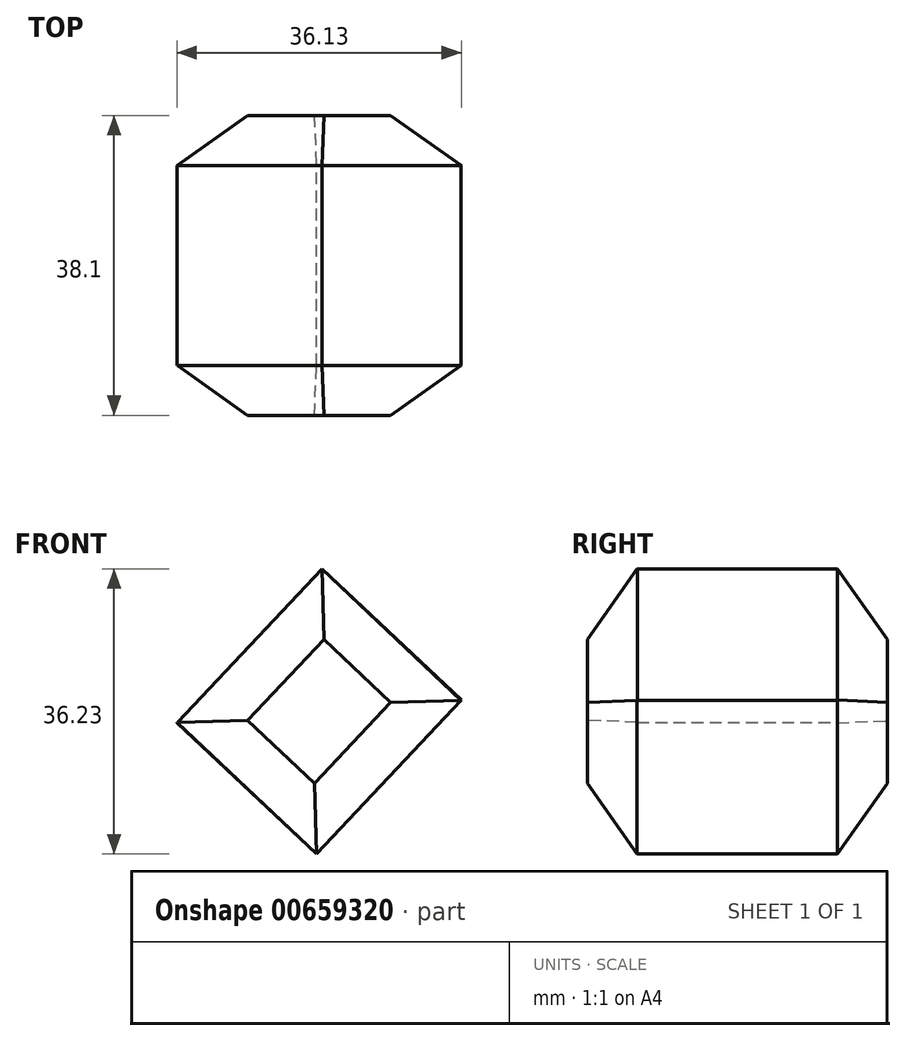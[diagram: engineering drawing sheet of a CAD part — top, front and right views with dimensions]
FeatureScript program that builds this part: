
annotation { "Feature Type Name" : "Feature", "Feature Type Description" : "" }
export const myFeature = defineFeature(function(context is Context, id is Id, definition is map)
    precondition{}
    {
        {
            var Q0;
            Q0=qCreatedBy(makeId("Front.planeOp"),FACE);
            var sketch = newSketch(context, id + "F0", { "sketchPlane" : qUnion([Q0])});
            skCircle(sketch, "E0", {"center": v(-16.93, -16.93) * mm, "radius": 23.2 * mm});
            skSolve(sketch);
        }
        {
            var Q0;
            Q0=makeQuery(id+"F0.imprint","IMPRINT",FACE,{"disambiguationData":[TD([[makeQuery(id+"F0.imprint","IMPRINT",EDGE,{"derivedFrom":sQuery(id+"F0.wireOp",EDGE,"E0")}),1.0]])]});
            extrude(context, id + "F1", {"entities" : qUnion([Q0]), "depth" : 12.7 * mm, "offsetDistance" : 25.4 * mm});
        }
        {
            var Q0;
            Q0=makeQuery(id+"F1.opExtrude","CAP_FACE",FACE,{"disambiguationData":[OSD([sQuery(id+"F0.wireOp",EDGE,"E0")])],"isStart":true});
            var sketch = newSketch(context, id + "F2", { "sketchPlane" : qUnion([Q0])});
            skSolve(sketch);
        }
        {
            var Q0;
            Q0=qSketchRegion(id+"F2",true);
            var Q1;
            Q1=makeQuery(id+"F2.imprint","IMPRINT",FACE,{"disambiguationData":[TD([[makeQuery(id+"F2.imprint","IMPRINT",EDGE,{"derivedFrom":makeQuery(id+"F1.opExtrude","CAP_EDGE",EDGE,{"disambiguationData":[OSD([sQuery(id+"F0.wireOp",EDGE,"E0")])],"isStart":true})}),-1.0]])]});
            extrude(context, id + "F3", {"entities" : qUnion([Q0, Q1]), "operationType" : NewBodyOperationType.ADD, "depth" : 12.7 * mm, "offsetDistance" : 25.4 * mm});
        }
        {
            var Q0;
            Q0=makeQuery(id+"F3.opExtrude","CAP_FACE",FACE,{"disambiguationData":[OSD([sQuery(id+"F0.wireOp",EDGE,"E0")])],"isStart":false});
            var sketch = newSketch(context, id + "F4", { "sketchPlane" : qUnion([Q0])});
            skLineSegment(sketch, "E1", {"start": v(16.57, 1.2) * mm, "end": v(34.99, -18.36) * mm});
            skLineSegment(sketch, "E2", {"start": v(34.99, -18.36) * mm, "end": v(17.28, -35.04) * mm});
            skLineSegment(sketch, "E3", {"start": v(17.28, -35.04) * mm, "end": v(-1.14, -15.49) * mm});
            skLineSegment(sketch, "E4", {"start": v(-1.14, -15.49) * mm, "end": v(16.57, 1.2) * mm});
            skSolve(sketch);
        }
        {
            var Q0;
            Q0=makeQuery(id+"F1.opExtrude","CAP_FACE",FACE,{"disambiguationData":[OSD([sQuery(id+"F0.wireOp",EDGE,"E0")])],"isStart":false});
            var sketch = newSketch(context, id + "F5", { "sketchPlane" : qUnion([Q0])});
            skLineSegment(sketch, "E5", {"start": v(-16.59, 1.2) * mm, "end": v(1.14, -15.54) * mm});
            skLineSegment(sketch, "E6", {"start": v(1.14, -15.54) * mm, "end": v(-17.26, -35.04) * mm});
            skLineSegment(sketch, "E7", {"start": v(-17.26, -35.04) * mm, "end": v(-35, -18.3) * mm});
            skLineSegment(sketch, "E8", {"start": v(-35, -18.3) * mm, "end": v(-16.59, 1.2) * mm});
            skSolve(sketch);
        }
        {
            var Q0;
            Q0=makeQuery(id+"F4.imprint","IMPRINT",FACE,{"disambiguationData":[TD([[makeQuery(id+"F4.imprint","IMPRINT",EDGE,{"derivedFrom":sQuery(id+"F4.wireOp",EDGE,"E1")}),-1.0]])]});
            extrude(context, id + "F6", {"entities" : qUnion([Q0]), "operationType" : NewBodyOperationType.ADD, "depth" : 6.35 * mm, "offsetDistance" : 25.4 * mm});
        }
        {
            var Q0;
            Q0=makeQuery(id+"F5.imprint","IMPRINT",FACE,{"disambiguationData":[TD([[makeQuery(id+"F5.imprint","IMPRINT",EDGE,{"derivedFrom":sQuery(id+"F5.wireOp",EDGE,"E5")}),-1.0]])]});
            extrude(context, id + "F7", {"entities" : qUnion([Q0]), "operationType" : NewBodyOperationType.ADD, "depth" : 6.35 * mm, "offsetDistance" : 25.4 * mm});
        }
        {
            var Q0;
            Q0=makeQuery(id+"F6.opExtrude","CAP_FACE",FACE,{"disambiguationData":[OSD([sQuery(id+"F4.wireOp",EDGE,"E1"),sQuery(id+"F4.wireOp",EDGE,"E2"),sQuery(id+"F4.wireOp",EDGE,"E3"),sQuery(id+"F4.wireOp",EDGE,"E4")])],"isStart":false});
            chamfer(context, id + "F8", {"entities" : qUnion([Q0]), "width" : 6.35 * mm, "tangentPropagation" : true});
        }
        {
            var Q0;
            Q0=makeQuery(id+"F7.opExtrude","CAP_FACE",FACE,{"disambiguationData":[OSD([sQuery(id+"F5.wireOp",EDGE,"E5"),sQuery(id+"F5.wireOp",EDGE,"E6"),sQuery(id+"F5.wireOp",EDGE,"E7"),sQuery(id+"F5.wireOp",EDGE,"E8")])],"isStart":false});
            chamfer(context, id + "F9", {"entities" : qUnion([Q0]), "width" : 6.35 * mm, "tangentPropagation" : true});
        }
        {
            var Q0;
            {var subQ0=sQuery(id+"F0.wireOp",EDGE,"E0");var subQ1=makeQuery(id+"F1.opExtrude","CAP_FACE",FACE,{"disambiguationData":[OSD([subQ0])],"isStart":false});Q0=makeQuery(id+"F7.boolean.opBoolean","SPLIT",FACE,{"disambiguationData":[TD([subQ1,makeQuery(id+"FOe0SaatVae6QVj_1.opFillet","BLEND_FACE",FACE,{"disambiguationData":[OSD([subQ0]),TDD([makeQuery(id+"F1.opExtrude","CAP_EDGE",EDGE,{"disambiguationData":[OSD([subQ0])],"isStart":false})])]}),makeQuery(id+"F7.opExtrude","SWEPT_FACE",FACE,{"disambiguationData":[OSD([sQuery(id+"F5.wireOp",EDGE,"E5")])]}),makeQuery(id+"F7.opExtrude","SWEPT_FACE",FACE,{"disambiguationData":[OSD([sQuery(id+"F5.wireOp",EDGE,"E6")])]}),makeQuery(id+"F7.opExtrude","SWEPT_FACE",FACE,{"disambiguationData":[OSD([sQuery(id+"F5.wireOp",EDGE,"E8")])]})])],"derivedFrom":subQ1});}
            var Q1;
            {var subQ0=sQuery(id+"F0.wireOp",EDGE,"E0");var subQ1=makeQuery(id+"F1.opExtrude","CAP_FACE",FACE,{"disambiguationData":[OSD([subQ0])],"isStart":false});Q1=makeQuery(id+"F7.boolean.opBoolean","SPLIT",FACE,{"disambiguationData":[TD([subQ1,makeQuery(id+"FOe0SaatVae6QVj_1.opFillet","BLEND_FACE",FACE,{"disambiguationData":[OSD([subQ0]),TDD([makeQuery(id+"F1.opExtrude","CAP_EDGE",EDGE,{"disambiguationData":[OSD([subQ0])],"isStart":false})])]}),makeQuery(id+"F7.opExtrude","SWEPT_FACE",FACE,{"disambiguationData":[OSD([sQuery(id+"F5.wireOp",EDGE,"E5")])]}),makeQuery(id+"F7.opExtrude","SWEPT_FACE",FACE,{"disambiguationData":[OSD([sQuery(id+"F5.wireOp",EDGE,"E7")])]}),makeQuery(id+"F7.opExtrude","SWEPT_FACE",FACE,{"disambiguationData":[OSD([sQuery(id+"F5.wireOp",EDGE,"E8")])]})])],"derivedFrom":subQ1});}
            var Q2;
            {var subQ0=sQuery(id+"F0.wireOp",EDGE,"E0");var subQ1=makeQuery(id+"F1.opExtrude","CAP_FACE",FACE,{"disambiguationData":[OSD([subQ0])],"isStart":false});Q2=makeQuery(id+"F7.boolean.opBoolean","SPLIT",FACE,{"disambiguationData":[TD([subQ1,makeQuery(id+"FOe0SaatVae6QVj_1.opFillet","BLEND_FACE",FACE,{"disambiguationData":[OSD([subQ0]),TDD([makeQuery(id+"F1.opExtrude","CAP_EDGE",EDGE,{"disambiguationData":[OSD([subQ0])],"isStart":false})])]}),makeQuery(id+"F7.opExtrude","SWEPT_FACE",FACE,{"disambiguationData":[OSD([sQuery(id+"F5.wireOp",EDGE,"E6")])]}),makeQuery(id+"F7.opExtrude","SWEPT_FACE",FACE,{"disambiguationData":[OSD([sQuery(id+"F5.wireOp",EDGE,"E7")])]}),makeQuery(id+"F7.opExtrude","SWEPT_FACE",FACE,{"disambiguationData":[OSD([sQuery(id+"F5.wireOp",EDGE,"E8")])]})])],"derivedFrom":subQ1});}
            var Q3;
            {var subQ0=sQuery(id+"F0.wireOp",EDGE,"E0");var subQ1=makeQuery(id+"F1.opExtrude","CAP_FACE",FACE,{"disambiguationData":[OSD([subQ0])],"isStart":false});Q3=makeQuery(id+"F7.boolean.opBoolean","SPLIT",FACE,{"disambiguationData":[TD([subQ1,makeQuery(id+"FOe0SaatVae6QVj_1.opFillet","BLEND_FACE",FACE,{"disambiguationData":[OSD([subQ0]),TDD([makeQuery(id+"F1.opExtrude","CAP_EDGE",EDGE,{"disambiguationData":[OSD([subQ0])],"isStart":false})])]}),makeQuery(id+"F7.opExtrude","SWEPT_FACE",FACE,{"disambiguationData":[OSD([sQuery(id+"F5.wireOp",EDGE,"E5")])]}),makeQuery(id+"F7.opExtrude","SWEPT_FACE",FACE,{"disambiguationData":[OSD([sQuery(id+"F5.wireOp",EDGE,"E6")])]}),makeQuery(id+"F7.opExtrude","SWEPT_FACE",FACE,{"disambiguationData":[OSD([sQuery(id+"F5.wireOp",EDGE,"E7")])]})])],"derivedFrom":subQ1});}
            extrude(context, id + "F10", {"entities" : qUnion([Q0, Q1, Q2, Q3]), "operationType" : NewBodyOperationType.REMOVE, "oppositeDirection" : true, "depth" : 25.4 * mm, "offsetDistance" : 25.4 * mm});
        }
        {
            var Q0;
            {var subQ0=sQuery(id+"F0.wireOp",EDGE,"E0");var subQ1=makeQuery(id+"F3.opExtrude","CAP_FACE",FACE,{"disambiguationData":[OSD([subQ0])],"isStart":false});Q0=makeQuery(id+"F6.boolean.opBoolean","SPLIT",FACE,{"disambiguationData":[TD([subQ1,makeQuery(id+"FOe0SaatVae6QVj_1.opFillet","BLEND_FACE",FACE,{"disambiguationData":[OSD([subQ0]),TDD([makeQuery(id+"F3.opExtrude","CAP_EDGE",EDGE,{"disambiguationData":[OSD([subQ0])],"isStart":false})])]}),makeQuery(id+"F6.opExtrude","SWEPT_FACE",FACE,{"disambiguationData":[OSD([sQuery(id+"F4.wireOp",EDGE,"E1")])]}),makeQuery(id+"F6.opExtrude","SWEPT_FACE",FACE,{"disambiguationData":[OSD([sQuery(id+"F4.wireOp",EDGE,"E2")])]}),makeQuery(id+"F6.opExtrude","SWEPT_FACE",FACE,{"disambiguationData":[OSD([sQuery(id+"F4.wireOp",EDGE,"E4")])]})])],"derivedFrom":subQ1});}
            extrude(context, id + "F11", {"entities" : qUnion([Q0]), "operationType" : NewBodyOperationType.REMOVE, "oppositeDirection" : true, "depth" : 127 * mm, "offsetDistance" : 25.4 * mm});
        }
    });
